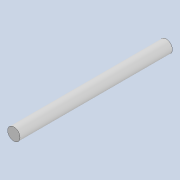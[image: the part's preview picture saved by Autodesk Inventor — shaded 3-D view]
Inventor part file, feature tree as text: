
AUTODESK INVENTOR PART (.ipt)
format: ipt  version: 2021 (Build 250183000, 183)  size: 72,704 bytes
history: native  units: mm
features: other x1, extrude x1, sketch x1
ambient origin geometry x8: Origin, YZ Plane, XZ Plane, XY Plane, X Axis, Y Axis, Z Axis, Center Point
bodies: Body1 (feature_tree)
feature tree (3):
  other  "Sólido1"
  extrude  "Extrusión1"  Depth=233.8mm TaperAngle=0.0deg
  sketch  "Boceto1"  dims[d0=19.0mm d1=233.8mm d2=0.0mm]
